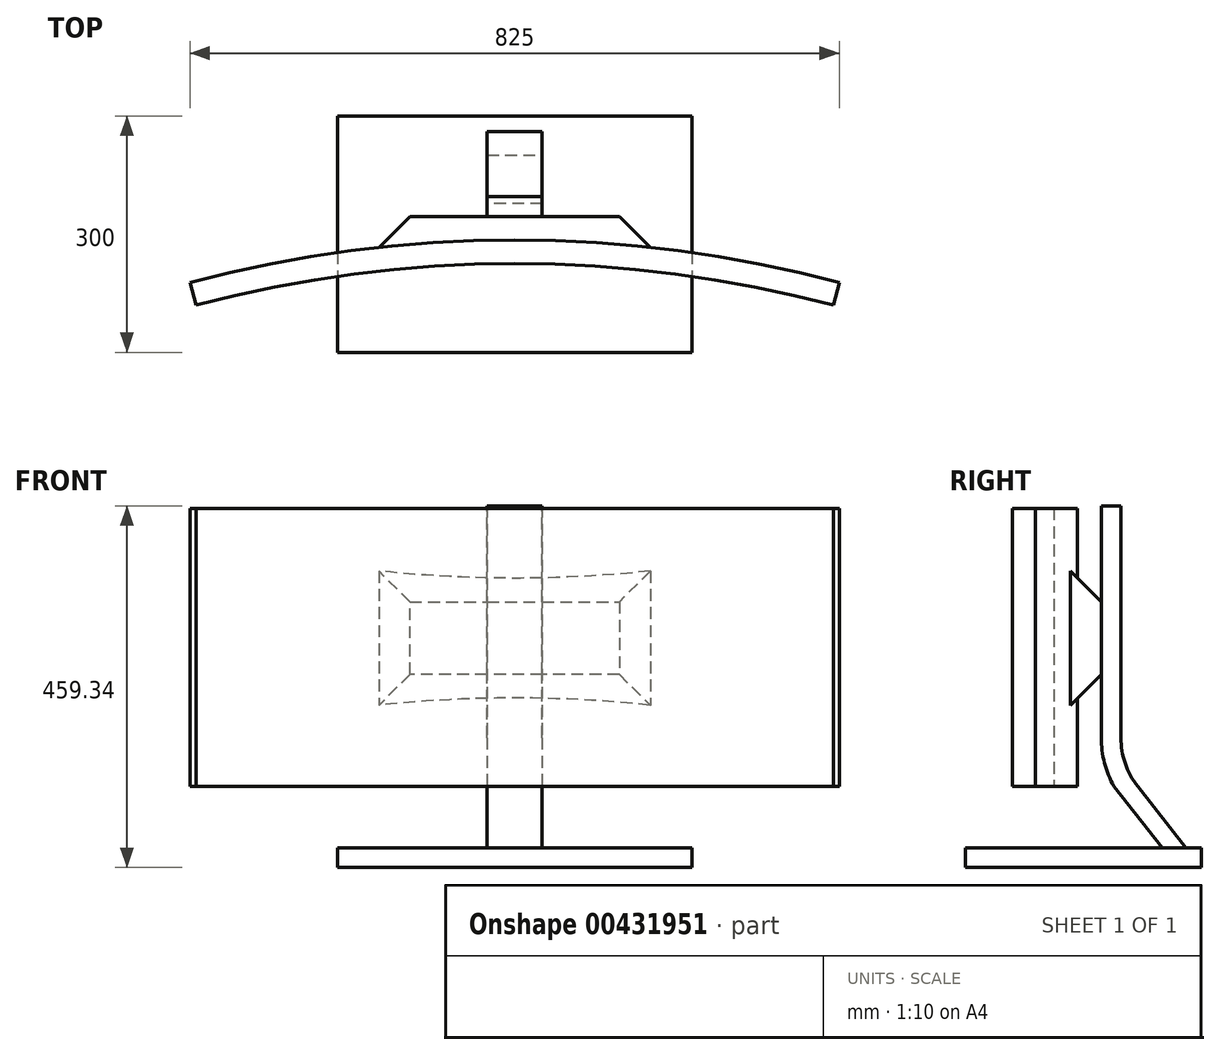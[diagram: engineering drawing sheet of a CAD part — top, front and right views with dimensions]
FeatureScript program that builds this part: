
annotation { "Feature Type Name" : "Feature", "Feature Type Description" : "" }
export const myFeature = defineFeature(function(context is Context, id is Id, definition is map)
    precondition{}
    {
        {
            var Q0;
            Q0=qCreatedBy(makeId("Top.planeOp"),FACE);
            var sketch = newSketch(context, id + "F0", { "sketchPlane" : qUnion([Q0])});
            skLineSegment(sketch, "E0", {"start": v(-412.5, -23.76) * mm, "end": v(-404.81, -52.76) * mm});
            skLineSegment(sketch, "E1", {"start": v(0, 0) * mm, "end": v(0, -1579.35) * mm, "construction": true});
            skArc(sketch, "E2", {"start": v(-412.5, -23.76) * mm, "mid": v(-208, 16.5) * mm, "end": v(0, 30) * mm});
            skArc(sketch, "E3", {"start": v(-404.81, -52.76) * mm, "mid": v(-204.12, -13.25) * mm, "end": v(0, 0) * mm});
            skLineSegment(sketch, "E4", {"start": v(-404.81, -52.76) * mm, "end": v(0, -1579.35) * mm, "construction": true});
            skArc(sketch, "E5.MirrorCS", {"start": v(412.5, -23.76) * mm, "mid": v(208, 16.5) * mm, "end": v(0, 30) * mm});
            skArc(sketch, "E6.MirrorCS", {"start": v(404.81, -52.76) * mm, "mid": v(204.12, -13.25) * mm, "end": v(0, 0) * mm});
            skLineSegment(sketch, "E7.MirrorCS", {"start": v(412.5, -23.76) * mm, "end": v(404.81, -52.76) * mm});
            skSolve(sketch);
        }
        {
            var Q0;
            Q0 = qSketchRegion(id + "F0", true);
            extrude(context, id + "F1", {"entities" : qUnion([Q0]), "depth" : 353 * mm, "offsetDistance" : 25 * mm});
        }
        {
            var Q0;
            Q0=qCreatedBy(makeId("Front.planeOp"),FACE);
            var sketch = newSketch(context, id + "F2", { "sketchPlane" : qUnion([Q0])});
            skLineSegment(sketch, "E8.bottom", {"start": v(208.03, 309.26) * mm, "end": v(-208.03, 309.26) * mm});
            skLineSegment(sketch, "E8.top", {"start": v(208.03, 67.17) * mm, "end": v(-208.03, 67.17) * mm});
            skLineSegment(sketch, "E8.left", {"start": v(208.03, 309.26) * mm, "end": v(208.03, 67.17) * mm});
            skLineSegment(sketch, "E8.right", {"start": v(-208.03, 309.26) * mm, "end": v(-208.03, 67.17) * mm});
            skPoint(sketch, "E8.middle", {"position": v(0, 188.22) * mm});
            skSolve(sketch);
        }
        {
            var Q0;
            Q0 = qSketchRegion(id + "F2", true);
            extrude(context, id + "F3", {"entities" : qUnion([Q0]), "operationType" : NewBodyOperationType.ADD, "oppositeDirection" : true, "depth" : 60 * mm, "offsetDistance" : 25 * mm});
        }
        {
            var Q0;
            Q0=makeQuery(id+"F3.opExtrude","CAP_EDGE",EDGE,{"disambiguationData":[OSD([sQuery(id+"F2.wireOp",EDGE,"E8.bottom")])],"isStart":false});
            var Q1;
            Q1=makeQuery(id+"F3.opExtrude","CAP_EDGE",EDGE,{"disambiguationData":[OSD([sQuery(id+"F2.wireOp",EDGE,"E8.right")])],"isStart":false});
            var Q2;
            Q2=makeQuery(id+"F3.opExtrude","CAP_EDGE",EDGE,{"disambiguationData":[OSD([sQuery(id+"F2.wireOp",EDGE,"E8.top")])],"isStart":false});
            var Q3;
            Q3=makeQuery(id+"F3.opExtrude","CAP_EDGE",EDGE,{"disambiguationData":[OSD([sQuery(id+"F2.wireOp",EDGE,"E8.left")])],"isStart":false});
            chamfer(context, id + "F4", {"entities" : qUnion([Q0, Q1, Q2, Q3]), "width" : 75 * mm, "tangentPropagation" : true});
        }
        {
            var Q0;
            Q0=qCreatedBy(makeId("Right.planeOp"),FACE);
            var sketch = newSketch(context, id + "F5", { "sketchPlane" : qUnion([Q0])});
            skLineSegment(sketch, "E9.0", {"start": v(60, 234.26) * mm, "end": v(60, 142.17) * mm});
            skLineSegment(sketch, "E10", {"start": v(60, 234.26) * mm, "end": v(60, 356.34) * mm});
            skLineSegment(sketch, "E11", {"start": v(60, 356.34) * mm, "end": v(85, 356.34) * mm});
            skLineSegment(sketch, "E12", {"start": v(85, 356.34) * mm, "end": v(85, 61.65) * mm});
            skArc(sketch, "E13", {"start": v(85, 61.65) * mm, "mid": v(90.49, 29.03) * mm, "end": v(106.35, 0) * mm});
            skLineSegment(sketch, "E14", {"start": v(106.35, 0) * mm, "end": v(187.42, -103) * mm});
            skLineSegment(sketch, "E15", {"start": v(187.42, -103) * mm, "end": v(157.37, -103) * mm});
            skLineSegment(sketch, "E16", {"start": v(157.37, -103) * mm, "end": v(76.3, 0) * mm});
            skLineSegment(sketch, "E17", {"start": v(60, 142.17) * mm, "end": v(60, 61.65) * mm});
            skArc(sketch, "E18", {"start": v(76.3, 0) * mm, "mid": v(64.15, 29.77) * mm, "end": v(60, 61.65) * mm});
            skLineSegment(sketch, "E19.0", {"start": v(-23.76, 353) * mm, "end": v(-52.76, 353) * mm});
            skSolve(sketch);
        }
        {
            var Q0;
            Q0 = qSketchRegion(id + "F5", true);
            extrude(context, id + "F6", {"entities" : qUnion([Q0]), "operationType" : NewBodyOperationType.ADD, "depth" : 35 * mm, "offsetDistance" : 25 * mm, "hasSecondDirection" : true, "secondDirectionOppositeDirection" : true, "secondDirectionDepth" : 35 * mm});
        }
        {
            var Q0;
            Q0=makeQuery(id+"F6.opExtrude","SWEPT_FACE",FACE,{"disambiguationData":[OSD([sQuery(id+"F5.wireOp",EDGE,"E15")])]});
            var sketch = newSketch(context, id + "F7", { "sketchPlane" : qUnion([Q0])});
            skLineSegment(sketch, "E20.bottom", {"start": v(225, -187.42) * mm, "end": v(-225, -187.42) * mm});
            skLineSegment(sketch, "E20.top", {"start": v(225, 112.58) * mm, "end": v(-225, 112.58) * mm});
            skLineSegment(sketch, "E20.left", {"start": v(225, -187.42) * mm, "end": v(225, 112.58) * mm});
            skLineSegment(sketch, "E20.right", {"start": v(-225, -187.42) * mm, "end": v(-225, 112.58) * mm});
            skLineSegment(sketch, "E21", {"start": v(0, -187.42) * mm, "end": v(0, -157.37) * mm, "construction": true});
            skSolve(sketch);
        }
        {
            var Q0;
            Q0 = qSketchRegion(id + "F7", true);
            extrude(context, id + "F8", {"entities" : qUnion([Q0]), "operationType" : NewBodyOperationType.ADD, "oppositeDirection" : true, "depth" : 25 * mm, "offsetDistance" : 25 * mm});
        }
    });
